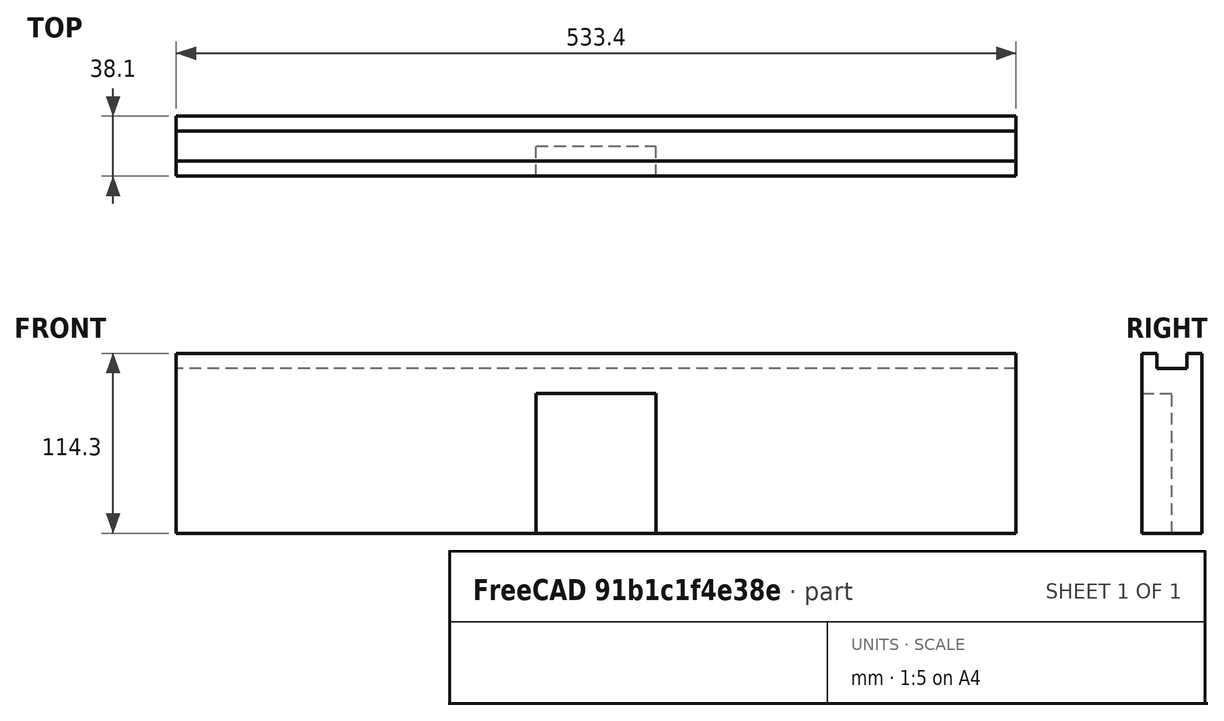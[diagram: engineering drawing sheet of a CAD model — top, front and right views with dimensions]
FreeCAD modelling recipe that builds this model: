
FCSTD DOCUMENT  (FreeCAD 0.20R29603 (Git))
Label: near_fence
License: All rights reserved
LicenseURL: http://en.wikipedia.org/wiki/All_rights_reserved
objects: TechDraw::DrawViewDimension×8, Sketcher::SketchObject×3, TechDraw::DrawProjGroupItem×3, PartDesign::Pocket×2, TechDraw::DrawProjGroup×2, PartDesign::Pad×1, PartDesign::Body×1, App::Part×1, TechDraw::DrawSVGTemplate×1, TechDraw::DrawViewSection×1, TechDraw::DrawPage×1
note: 10 computed .brp shape members not serialized (recipe doc carries the construction recipe); baked Part::Feature solids carry a one-line shape summary decoded from their .brp

FEATURE [Sketcher::SketchObject] Sketch
  FullyConstrained = true
  MapMode = 5
  Support = -> [XY_Plane002]
  sketch-geometry (5):
    g0: LineSegment StartX=-266.7 StartY=-19.05 StartZ=0 EndX=-266.7 EndY=19.05 EndZ=0
    g1: LineSegment StartX=-266.7 StartY=19.05 StartZ=0 EndX=266.7 EndY=19.05 EndZ=0
    g2: LineSegment StartX=266.7 StartY=19.05 StartZ=0 EndX=266.7 EndY=-19.05 EndZ=0
    g3: LineSegment StartX=266.7 StartY=-19.05 StartZ=0 EndX=-266.7 EndY=-19.05 EndZ=0
    g4: GeomPoint X=0 Y=0 Z=0
  constraints (12):
    c: Coincident(g0,g1)
    c: Coincident(g1,g2)
    c: Coincident(g2,g3)
    c: Coincident(g3,g0)
    c: Horizontal(g1)
    c: Horizontal(g3)
    c: Vertical(g0)
    c: Vertical(g2)
    c: Symmetric(g1,g0,g4)
    c: Coincident(g4,g-1)
    c: DistanceX(g1,g1) = 533.4
    c: DistanceY(g2,g2) = 38.1
FEATURE [PartDesign::Pad] Pad  label="Base"
  Direction = (0,0,1)
  Length = 114.3
  Length2 = 10
  Profile = -> Sketch
  ReferenceAxis = -> Sketch [N_Axis]
  Type = 0
FEATURE [Sketcher::SketchObject] Sketch001
  ExternalGeometry = -> [Pad]
  FullyConstrained = false
  MapMode = 5
  Placement = pos=(0,0,114.3) rot=(0,0,1;0rad)
  Support = -> [Pad]
  sketch-geometry (5):
    g0: LineSegment StartX=381 StartY=-9.525 StartZ=0 EndX=381 EndY=9.525 EndZ=0
    g1: LineSegment StartX=381 StartY=9.525 StartZ=0 EndX=-381 EndY=9.525 EndZ=0
    g2: LineSegment StartX=-381 StartY=9.525 StartZ=0 EndX=-381 EndY=-9.525 EndZ=0
    g3: LineSegment StartX=-381 StartY=-9.525 StartZ=0 EndX=381 EndY=-9.525 EndZ=0
    g4: GeomPoint X=-1.77e-14 Y=-1e-16 Z=0
  constraints (11):
    c: Coincident(g0,g1)
    c: Coincident(g1,g2)
    c: Coincident(g2,g3)
    c: Coincident(g3,g0)
    c: Horizontal(g1)
    c: Horizontal(g3)
    c: Symmetric(g1,g0,g4)
    c: Tangent(g-3,g2)
    c: Tangent(g0,g-4)
    c: Coincident(g4,g-1)
    c: DistanceY(g2,g2) = 19.05
FEATURE [PartDesign::Pocket] Pocket  label="Top T-Track Dado"
  BaseFeature = -> Pad
  Direction = (0,0,-1)
  Length = 9.525
  Length2 = 5
  Profile = -> Sketch001
  ReferenceAxis = -> Sketch001 [N_Axis]
  Type = 0
FEATURE [Sketcher::SketchObject] Sketch003
  ExternalGeometry = -> [Pocket]
  FullyConstrained = true
  MapMode = 5
  Placement = pos=(0,-19.05,0) rot=(1,0,0;1.5708rad)
  sketch-geometry (5):
    g0: LineSegment StartX=-38.1 StartY=88.9 StartZ=0 EndX=-38.1 EndY=0 EndZ=0
    g1: LineSegment StartX=-38.1 StartY=0 StartZ=0 EndX=38.1 EndY=0 EndZ=0
    g2: LineSegment StartX=38.1 StartY=0 StartZ=0 EndX=38.1 EndY=88.9 EndZ=0
    g3: LineSegment StartX=38.1 StartY=88.9 StartZ=0 EndX=-38.1 EndY=88.9 EndZ=0
    g4: GeomPoint X=0 Y=44.45 Z=0
  constraints (12):
    c: Coincident(g0,g1)
    c: Coincident(g1,g2)
    c: Coincident(g2,g3)
    c: Coincident(g3,g0)
    c: Horizontal(g3)
    c: Vertical(g0)
    c: Vertical(g2)
    c: Symmetric(g1,g0,g4)
    c: PointOnObject(g4,g-2)
    c: DistanceY(g0,g0) = 88.9
    c: DistanceX(g3,g3) = 76.2
    c: Tangent(g1,g-3)
FEATURE [PartDesign::Pocket] Pocket002
  BaseFeature = -> Pocket
  Direction = (0,1,-2e-16)
  Length = 19.05
  Length2 = 5
  Profile = -> Sketch003
  ReferenceAxis = -> Sketch003 [N_Axis]
  Type = 0
FEATURE [PartDesign::Body] PocketBody
  Group = -> [Sketch,Pad,Sketch001,Pocket,Sketch003,Pocket002]
  Origin = -> Origin002
  Tip = -> Pocket002
FEATURE [App::Part] Part
  Group = -> [PocketBody]
  Origin = -> Origin001
FEATURE [TechDraw::DrawSVGTemplate] Template
  Height = 297
  Orientation = 1
  Width = 420
FEATURE [TechDraw::DrawProjGroupItem] ProjItem  label="Front"
  CoarseView = false
  Direction = (0,-1,0)
  Focus = 100
  HardHidden = false
  IsoCount = 0
  IsoHidden = false
  IsoVisible = false
  LockPosition = true
  Perspective = false
  Rotation = 0
  RotationVector = (1,0,0)
  Scale = 0.3
  ScaleType = 2
  SeamHidden = false
  SeamVisible = true
  SmoothHidden = false
  SmoothVisible = true
  Type = 0
  X = 0
  XDirection = (1,0,0)
  Y = 0
FEATURE [TechDraw::DrawProjGroup] ProjGroup
  Anchor = -> ProjItem
  AutoDistribute = true
  LockPosition = false
  ProjectionType = 0
  Rotation = 0
  Scale = 0.3
  ScaleType = 0
  Views = -> [ProjItem]
  X = 210
  Y = 148.5
  spacingX = 15.0812
  spacingY = 15.0812
FEATURE [TechDraw::DrawProjGroupItem] ProjItem001  label="Front001"
  CoarseView = false
  Direction = (0,-1,0)
  Focus = 100
  HardHidden = false
  IsoCount = 0
  IsoHidden = false
  IsoVisible = false
  LockPosition = true
  Perspective = false
  Rotation = 0
  RotationVector = (1,0,0)
  Scale = 0.3
  ScaleType = 2
  SeamHidden = false
  SeamVisible = true
  SmoothHidden = false
  SmoothVisible = true
  Source = -> [Part]
  Type = 0
  X = 0
  XDirection = (1,0,0)
  Y = 0
FEATURE [TechDraw::DrawProjGroupItem] ProjItem003  label="FrontTopRight"
  CoarseView = false
  Direction = (0.57735,-0.57735,0.57735)
  Focus = 100
  HardHidden = false
  IsoCount = 0
  IsoHidden = false
  IsoVisible = false
  LockPosition = false
  Perspective = false
  Rotation = 0
  RotationVector = (1,0,0)
  Scale = 0.3
  ScaleType = 2
  SeamHidden = false
  SeamVisible = true
  SmoothHidden = false
  SmoothVisible = true
  Source = -> [Part]
  Type = 7
  X = 226.071
  XDirection = (0.707107,0.707107,0)
  Y = 95.3976
FEATURE [TechDraw::DrawProjGroup] ProjGroup001
  Anchor = -> ProjItem001
  AutoDistribute = true
  LockPosition = false
  ProjectionType = 0
  Rotation = 0
  Scale = 0.3
  ScaleType = 0
  Source = -> [Part]
  Views = -> [ProjItem001,ProjItem003]
  X = 116.834
  Y = 133.321
  spacingX = 15.0812
  spacingY = 15.0812
FEATURE [TechDraw::DrawViewSection] SectionView  label="Section  - "
  BaseView = -> ProjItem001
  CoarseView = false
  CutSurfaceDisplay = 2
  Direction = (-1,0,0)
  FileGeomPattern = <path>
  FileHatchPattern = <path>
  Focus = 100
  FuseBeforeCut = false
  HardHidden = false
  HatchScale = 1
  IsoCount = 0
  IsoHidden = false
  IsoVisible = false
  LockPosition = false
  NameGeomPattern = Diamond
  Perspective = false
  Rotation = 0
  Scale = 0.3
  ScaleType = 2
  SeamHidden = false
  SeamVisible = true
  SectionDirection = 0
  SectionNormal = (-1,0,0)
  SectionOrigin = (0,0,57.15)
  SmoothHidden = false
  SmoothVisible = true
  Source = -> [Part]
  X = 240.194
  XDirection = (0,-1,0)
  Y = 133.853
FEATURE [TechDraw::DrawViewDimension] Dimension
  AngleOverride = false
  Arbitrary = false
  ArbitraryTolerances = false
  EqualTolerance = true
  ExtensionAngle = 0
  FormatSpec = %.2w
  FormatSpecOverTolerance = %+.2w
  FormatSpecUnderTolerance = %+.2w
  Inverted = false
  LineAngle = 0
  LockPosition = false
  MeasureType = 1
  OverTolerance = 0
  References2D = -> [ProjItem001]
  Rotation = 0
  Scale = 0.3
  ScaleType = 0
  TheoreticalExact = false
  Type = 1
  UnderTolerance = 0
  X = 12.4187
  Y = 23.9652
FEATURE [TechDraw::DrawViewDimension] Dimension001
  AngleOverride = false
  Arbitrary = false
  ArbitraryTolerances = false
  EqualTolerance = true
  ExtensionAngle = 0
  FormatSpec = %.2w
  FormatSpecOverTolerance = %+.2w
  FormatSpecUnderTolerance = %+.2w
  Inverted = false
  LineAngle = 0
  LockPosition = false
  MeasureType = 1
  OverTolerance = 0
  References2D = -> [ProjItem001]
  Rotation = 0
  Scale = 0.3
  ScaleType = 0
  TheoreticalExact = false
  Type = 2
  UnderTolerance = 0
  X = -90.6113
  Y = -0.752159
FEATURE [TechDraw::DrawViewDimension] Dimension002
  AngleOverride = false
  Arbitrary = false
  ArbitraryTolerances = false
  EqualTolerance = true
  ExtensionAngle = 0
  FormatSpec = %.2w
  FormatSpecOverTolerance = %+.2w
  FormatSpecUnderTolerance = %+.2w
  Inverted = false
  LineAngle = 0
  LockPosition = false
  MeasureType = 1
  OverTolerance = 0
  References2D = -> [ProjItem001]
  Rotation = 0
  Scale = 0.3
  ScaleType = 0
  TheoreticalExact = false
  Type = 1
  UnderTolerance = 0
  X = -46.0229
  Y = -27.2869
FEATURE [TechDraw::DrawViewDimension] Dimension003
  AngleOverride = false
  Arbitrary = false
  ArbitraryTolerances = false
  EqualTolerance = true
  ExtensionAngle = 0
  FormatSpec = %.2w
  FormatSpecOverTolerance = %+.2w
  FormatSpecUnderTolerance = %+.2w
  Inverted = false
  LineAngle = 0
  LockPosition = false
  MeasureType = 1
  OverTolerance = 0
  References2D = -> [ProjItem001]
  Rotation = 0
  Scale = 0.3
  ScaleType = 0
  TheoreticalExact = false
  Type = 2
  UnderTolerance = 0
  X = -22.0313
  Y = 0.587058
FEATURE [TechDraw::DrawViewDimension] Dimension004
  AngleOverride = false
  Arbitrary = false
  ArbitraryTolerances = false
  EqualTolerance = true
  ExtensionAngle = 0
  FormatSpec = %.2w
  FormatSpecOverTolerance = %+.2w
  FormatSpecUnderTolerance = %+.2w
  Inverted = false
  LineAngle = 0
  LockPosition = false
  MeasureType = 1
  OverTolerance = 0
  References2D = -> [ProjItem001]
  Rotation = 0
  Scale = 0.3
  ScaleType = 0
  TheoreticalExact = false
  Type = 1
  UnderTolerance = 0
  X = 7.57238
  Y = 14.5278
FEATURE [TechDraw::DrawViewDimension] Dimension005
  AngleOverride = false
  Arbitrary = false
  ArbitraryTolerances = false
  EqualTolerance = true
  ExtensionAngle = 0
  FormatSpec = %.2w
  FormatSpecOverTolerance = %+.2w
  FormatSpecUnderTolerance = %+.2w
  Inverted = false
  LineAngle = 0
  LockPosition = false
  MeasureType = 1
  OverTolerance = 0
  References2D = -> [SectionView]
  Rotation = 0
  Scale = 0.3
  ScaleType = 0
  TheoreticalExact = false
  Type = 1
  UnderTolerance = 0
  X = 19.0189
  Y = 10.1845
FEATURE [TechDraw::DrawViewDimension] Dimension006
  AngleOverride = false
  Arbitrary = false
  ArbitraryTolerances = false
  EqualTolerance = true
  ExtensionAngle = 0
  FormatSpec = %.2w
  FormatSpecOverTolerance = %+.2w
  FormatSpecUnderTolerance = %+.2w
  Inverted = false
  LineAngle = 0
  LockPosition = false
  MeasureType = 1
  OverTolerance = 0
  References2D = -> [SectionView]
  Rotation = 0
  Scale = 0.3
  ScaleType = 0
  TheoreticalExact = false
  Type = 1
  UnderTolerance = 0
  X = 16.8015
  Y = 38.149
FEATURE [TechDraw::DrawViewDimension] Dimension007
  AngleOverride = false
  Arbitrary = false
  ArbitraryTolerances = false
  EqualTolerance = true
  ExtensionAngle = 0
  FormatSpec = %.2w
  FormatSpecOverTolerance = %+.2w
  FormatSpecUnderTolerance = %+.2w
  Inverted = false
  LineAngle = 0
  LockPosition = false
  MeasureType = 1
  OverTolerance = 0
  References2D = -> [SectionView]
  Rotation = 0
  Scale = 0.3
  ScaleType = 0
  TheoreticalExact = false
  Type = 2
  UnderTolerance = 0
  X = 24.6194
  Y = 33.6573
FEATURE [TechDraw::DrawPage] Page
  KeepUpdated = true
  NextBalloonIndex = 1
  ProjectionType = 0
  Scale = 0.3
  Template = -> Template
  Views = -> [ProjGroup,ProjGroup001,SectionView,Dimension,Dimension001,Dimension002,Dimension003,Dimension004,Dimension005,Dimension006,Dimension007]
note: 2 file-system paths scrubbed to <path> (originals preserved in the JSON sidecar)
